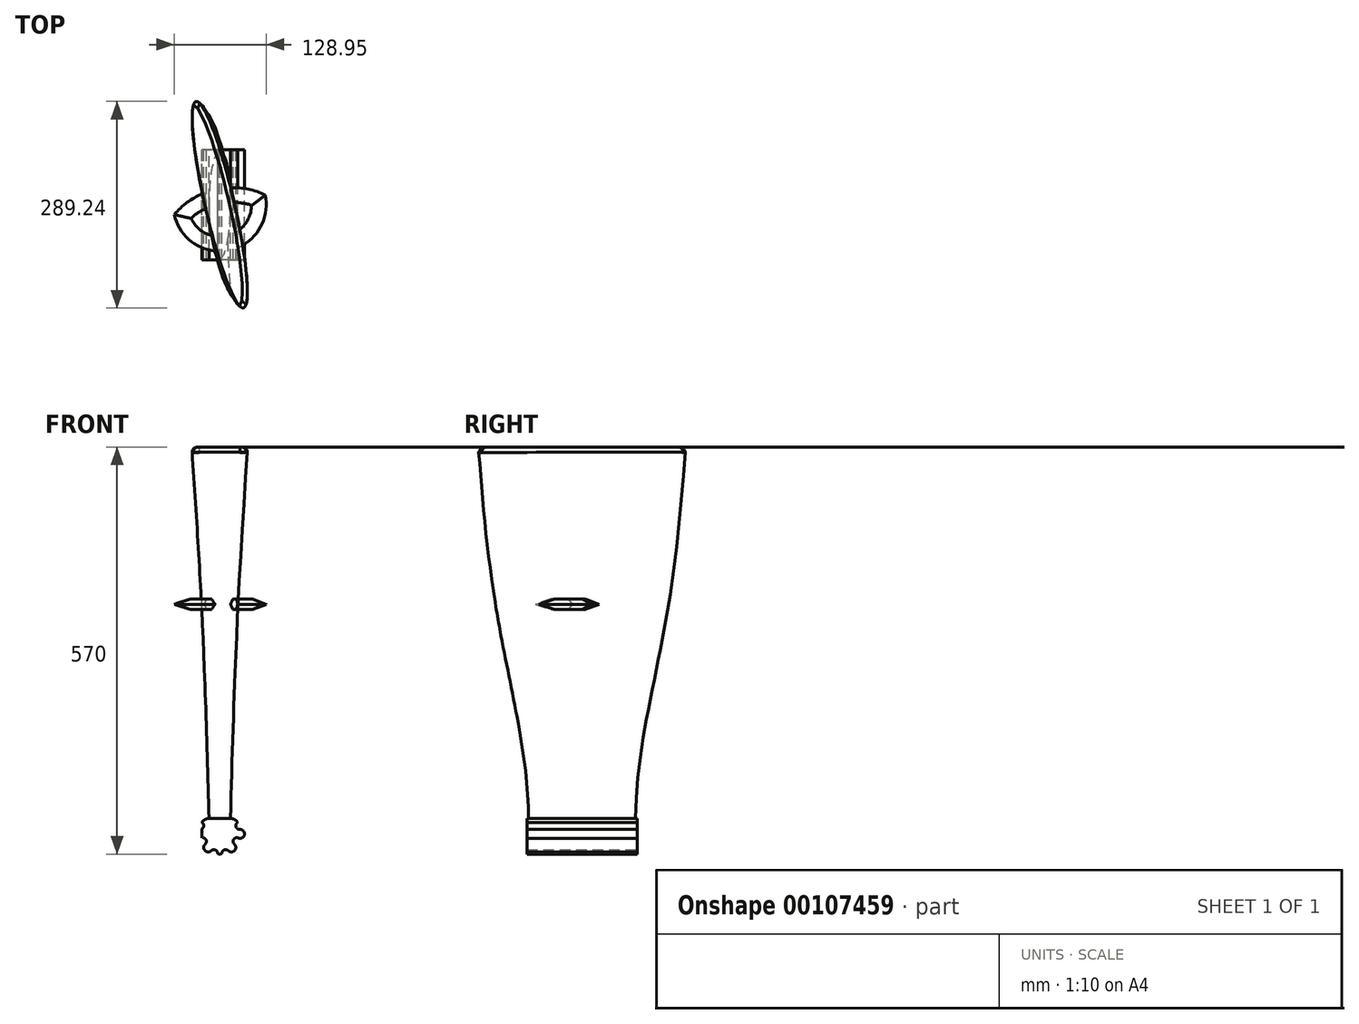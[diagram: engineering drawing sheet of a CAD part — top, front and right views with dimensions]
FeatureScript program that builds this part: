
annotation { "Feature Type Name" : "Feature", "Feature Type Description" : "" }
export const myFeature = defineFeature(function(context is Context, id is Id, definition is map)
    precondition{}
    {
        {
            var Q0;
            Q0=qCreatedBy(makeId("Top.planeOp"),FACE);
            var sketch = newSketch(context, id + "F0", { "sketchPlane" : qUnion([Q0])});
            skEllipse(sketch, "E0", {"center": v(0, 0) * mm, "majorRadius": 75 * mm, "minorRadius": 15 * mm, "majorAxis": v(0, -1)});
            skSolve(sketch);
        }
        {
            var Q0;
            Q0=qCreatedBy(makeId("Right.planeOp"),FACE);
            var sketch = newSketch(context, id + "F1", { "sketchPlane" : qUnion([Q0])});
            skLineSegment(sketch, "E1", {"start": v(0, -69.03) * mm, "end": v(0, 530.97) * mm});
            skSolve(sketch);
        }
        {
            var Q0;
            Q0=qCreatedBy(makeId("Top.planeOp"),FACE);
            cPlane(context, id + "F2", {"entities" : qUnion([Q0]), "cplaneType" : CPlaneType.OFFSET, "offset" : 300 * mm, "width" : 150 * mm, "height" : 150 * mm});
        }
        {
            var Q0;
            Q0=qCreatedBy(id+"F2.planeOp",FACE);
            cPlane(context, id + "F3", {"entities" : qUnion([Q0]), "cplaneType" : CPlaneType.OFFSET, "offset" : 220 * mm, "width" : 150 * mm, "height" : 150 * mm});
        }
        {
            var Q0;
            Q0=qCreatedBy(id+"F2.planeOp",FACE);
            var sketch = newSketch(context, id + "F4", { "sketchPlane" : qUnion([Q0])});
            skLineSegment(sketch, "E2", {"start": v(0, 0) * mm, "end": v(-15.27, 105.59) * mm});
            skLineSegment(sketch, "E3", {"start": v(-15.27, 105.59) * mm, "end": v(15.28, -105.68) * mm, "construction": true});
            skEllipse(sketch, "E4", {"center": v(0, 0) * mm, "majorRadius": 122.46 * mm, "minorRadius": 18.67 * mm, "majorAxis": v(-0.15, 0.99)});
            skSolve(sketch);
        }
        {
            var Q0;
            Q0=qCreatedBy(id+"F3.planeOp",FACE);
            var sketch = newSketch(context, id + "F5", { "sketchPlane" : qUnion([Q0])});
            skLineSegment(sketch, "E5", {"start": v(0, 0) * mm, "end": v(-31.02, 124.83) * mm, "construction": true});
            skLineSegment(sketch, "E6", {"start": v(0, 0) * mm, "end": v(31.81, -128) * mm, "construction": true});
            skEllipse(sketch, "E7", {"center": v(0, 0) * mm, "majorRadius": 149 * mm, "minorRadius": 20.42 * mm, "majorAxis": v(-0.23, 0.97)});
            skSolve(sketch);
        }
        {
            var Q0;
            Q0=makeQuery(id+"F0.imprint","IMPRINT",FACE,{"disambiguationData":[TD([[makeQuery(id+"F0.imprint","IMPRINT",EDGE,{"derivedFrom":sQuery(id+"F0.wireOp",EDGE,"E0")}),1.0]])]});
            var Q1;
            Q1=makeQuery(id+"F4.imprint","IMPRINT",FACE,{"disambiguationData":[TD([[makeQuery(id+"F4.imprint","IMPRINT",EDGE,{"derivedFrom":sQuery(id+"F4.wireOp",EDGE,"E4")}),1.0]])]});
            var Q2;
            Q2=makeQuery(id+"F5.imprint","IMPRINT",FACE,{"disambiguationData":[TD([[makeQuery(id+"F5.imprint","IMPRINT",EDGE,{"derivedFrom":sQuery(id+"F5.wireOp",EDGE,"E7")}),1.0]])]});
            loft(context, id + "F6", {"sheetProfilesArray" : [{ "sheetProfileEntities" : qUnion([Q0]) }, { "sheetProfileEntities" : qUnion([Q1]) }, { "sheetProfileEntities" : qUnion([Q2]) }]});
        }
        {
            var Q0;
            Q0=makeQuery(id+"F6.opLoft","MID_CAP_EDGE",EDGE,{"disambiguationData":[OSD([sQuery(id+"F0.wireOp",EDGE,"E0"),sQuery(id+"F5.wireOp",EDGE,"E7")])],"capPos":2.0});
            fillet(context, id + "F7", {"entities" : qUnion([Q0]), "radius" : 7 * mm, "tangentPropagation" : true, "allowEdgeOverflow" : false});
        }
        {
            var Q0;
            Q0=qCreatedBy(id+"F2.planeOp",FACE);
            var sketch = newSketch(context, id + "F8", { "sketchPlane" : qUnion([Q0])});
            skLineSegment(sketch, "E8", {"start": v(0, 0) * mm, "end": v(-63.75, -13.7) * mm});
            skLineSegment(sketch, "E9", {"start": v(0, 0) * mm, "end": v(63.75, 13.7) * mm});
            skArc(sketch, "E10", {"start": v(-63.75, -13.7) * mm, "mid": v(13.7, -63.75) * mm, "end": v(63.75, 13.7) * mm});
            skArc(sketch, "E11", {"start": v(63.75, 13.7) * mm, "mid": v(-4.61, 21.47) * mm, "end": v(-63.75, -13.7) * mm});
            skSolve(sketch);
        }
        {
            var Q0;
            Q0 = qSketchRegion(id + "F8", true);
            extrude(context, id + "F9", {"entities" : qUnion([Q0]), "operationType" : NewBodyOperationType.ADD, "endBound" : BoundingType.SYMMETRIC, "depth" : 15 * mm, "hasDraft" : true, "draftAngle" : 70 * degree, "draftPullDirection" : true});
        }
        {
            var Q0;
            Q0=qCreatedBy(makeId("Front.planeOp"),FACE);
            var sketch = newSketch(context, id + "F10", { "sketchPlane" : qUnion([Q0])});
            skLineSegment(sketch, "E12", {"start": v(25, 0) * mm, "end": v(-25, 0) * mm});
            skLineSegment(sketch, "E13.top", {"start": v(25, -50) * mm, "end": v(-25, -50) * mm});
            skLineSegment(sketch, "E13.left", {"start": v(25, 0) * mm, "end": v(25, -50) * mm});
            skLineSegment(sketch, "E13.right", {"start": v(-25, 0) * mm, "end": v(-25, -50) * mm});
            skLineSegment(sketch, "E14", {"start": v(0, 0) * mm, "end": v(0, -66.72) * mm, "construction": true});
            skArc(sketch, "E15", {"start": v(25, -5.65) * mm, "mid": v(20.66, -1.6) * mm, "end": v(14.93, 0) * mm});
            skArc(sketch, "E16", {"start": v(25, -5.65) * mm, "mid": v(22.67, -11.71) * mm, "end": v(28.03, -15.38) * mm});
            skArc(sketch, "E17", {"start": v(26.01, -27.37) * mm, "mid": v(34.63, -22.65) * mm, "end": v(28.03, -15.38) * mm});
            skArc(sketch, "E18", {"start": v(26.01, -27.37) * mm, "mid": v(19.57, -29.35) * mm, "end": v(20.42, -36.04) * mm});
            skArc(sketch, "E19", {"start": v(11.85, -45.15) * mm, "mid": v(20.74, -44.93) * mm, "end": v(20.42, -36.04) * mm});
            skArc(sketch, "E20", {"start": v(11.85, -45.15) * mm, "mid": v(5.99, -44.19) * mm, "end": v(3, -49.32) * mm});
            skArc(sketch, "E21.trimOffspring", {"start": v(3, -49.32) * mm, "mid": v(1.5, -49.7) * mm, "end": v(0, -50) * mm});
            skArc(sketch, "E22.MirrorCS", {"start": v(-3, -49.32) * mm, "mid": v(-1.5, -49.7) * mm, "end": v(0, -50) * mm});
            skArc(sketch, "E23.MirrorCS", {"start": v(-11.85, -45.15) * mm, "mid": v(-5.99, -44.19) * mm, "end": v(-3, -49.32) * mm});
            skArc(sketch, "E24.MirrorCS", {"start": v(-11.85, -45.15) * mm, "mid": v(-20.74, -44.93) * mm, "end": v(-20.42, -36.04) * mm});
            skArc(sketch, "E25.MirrorCS", {"start": v(-26.01, -27.37) * mm, "mid": v(-19.57, -29.35) * mm, "end": v(-20.42, -36.04) * mm});
            skArc(sketch, "E26.MirrorCS", {"start": v(-26.01, -27.37) * mm, "mid": v(-34.63, -22.65) * mm, "end": v(-28.03, -15.38) * mm});
            skArc(sketch, "E27.MirrorCS", {"start": v(-25, -5.65) * mm, "mid": v(-22.67, -11.71) * mm, "end": v(-28.03, -15.38) * mm});
            skArc(sketch, "E28.MirrorCS", {"start": v(-25, -5.65) * mm, "mid": v(-20.66, -1.6) * mm, "end": v(-14.93, 0) * mm});
            skSolve(sketch);
        }
        {
            var Q0;
            {var subQ5=sQuery(id+"F10.wireOp",EDGE,"E15");Q0=makeQuery(id+"F10.imprint","IMPRINT",FACE,{"disambiguationData":[TD([[makeQuery(id+"F10.imprint","IMPRINT",EDGE,{"derivedFrom":subQ5}),1.0]])]});}
            var Q1;
            {var subQ5=sQuery(id+"F10.wireOp",EDGE,"E26.MirrorCS");Q1=makeQuery(id+"F10.imprint","IMPRINT",FACE,{"disambiguationData":[TD([[makeQuery(id+"F10.imprint","IMPRINT",EDGE,{"derivedFrom":subQ5}),-1.0]])]});}
            var Q2;
            {var subQ5=sQuery(id+"F10.wireOp",EDGE,"E17");Q2=makeQuery(id+"F10.imprint","IMPRINT",FACE,{"disambiguationData":[TD([[makeQuery(id+"F10.imprint","IMPRINT",EDGE,{"derivedFrom":subQ5}),1.0]])]});}
            extrude(context, id + "F11", {"entities" : qUnion([Q0, Q1, Q2]), "operationType" : NewBodyOperationType.ADD, "endBound" : BoundingType.SYMMETRIC, "depth" : 154.45 * mm});
        }
    });
